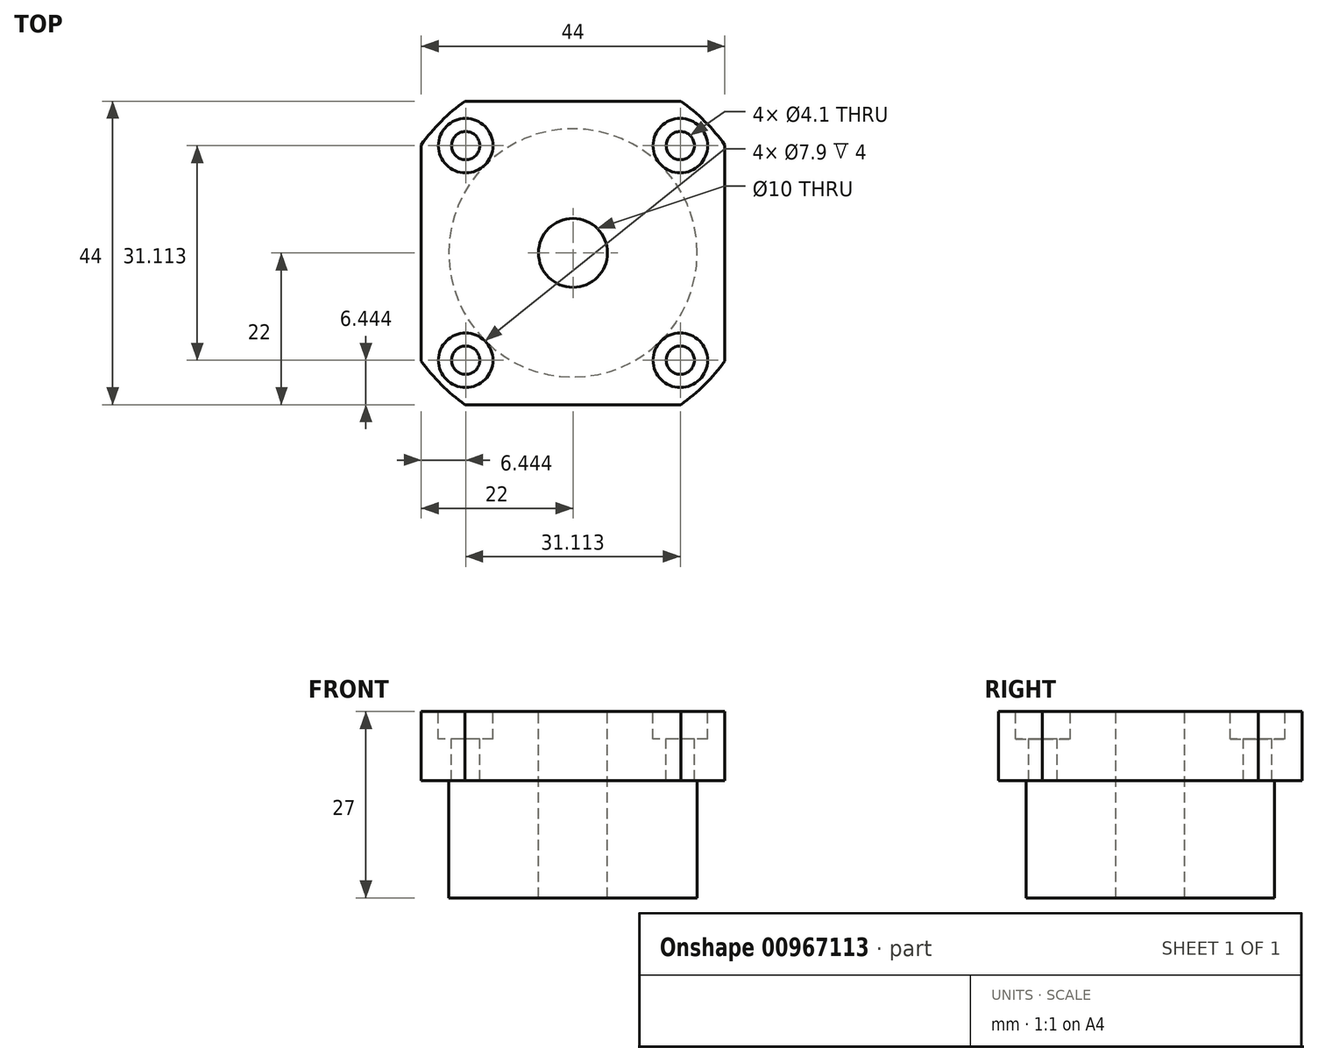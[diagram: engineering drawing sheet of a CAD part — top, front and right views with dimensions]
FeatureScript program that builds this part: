
annotation { "Feature Type Name" : "Feature", "Feature Type Description" : "" }
export const myFeature = defineFeature(function(context is Context, id is Id, definition is map)
    precondition{}
    {
        {
            var Q0;
            Q0=qCreatedBy(makeId("Top.planeOp"),FACE);
            var sketch = newSketch(context, id + "F0", { "sketchPlane" : qUnion([Q0])});
            skLineSegment(sketch, "E0.bottom", {"start": v(0, 0) * mm, "end": v(44, 0) * mm});
            skLineSegment(sketch, "E0.top", {"start": v(0, -44) * mm, "end": v(44, -44) * mm});
            skLineSegment(sketch, "E0.left", {"start": v(0, 0) * mm, "end": v(0, -44) * mm});
            skLineSegment(sketch, "E0.right", {"start": v(44, 0) * mm, "end": v(44, -44) * mm});
            skCircle(sketch, "E1", {"center": v(22, -22) * mm, "radius": 18 * mm});
            skPoint(sketch, "E1.centerSnap0", {"position": v(22, 0) * mm});
            skPoint(sketch, "E1.centerSnap1", {"position": v(0, -22) * mm});
            skCircle(sketch, "E2", {"center": v(22, -22) * mm, "radius": 27 * mm});
            skCircle(sketch, "E3", {"center": v(22, -22) * mm, "radius": 22 * mm, "construction": true});
            skLineSegment(sketch, "E4", {"start": v(22, -22) * mm, "end": v(0, 0) * mm, "construction": true});
            skCircle(sketch, "E5", {"center": v(6.44, -6.44) * mm, "radius": 2.05 * mm});
            skCircle(sketch, "E6", {"center": v(6.44, -6.44) * mm, "radius": 3.95 * mm});
            skCircle(sketch, "E7.1.0", {"center": v(6.44, -37.56) * mm, "radius": 2.05 * mm});
            skCircle(sketch, "E7.1.1", {"center": v(6.44, -37.56) * mm, "radius": 3.95 * mm});
            skCircle(sketch, "E7.2.0", {"center": v(37.56, -37.56) * mm, "radius": 2.05 * mm});
            skCircle(sketch, "E7.2.1", {"center": v(37.56, -37.56) * mm, "radius": 3.95 * mm});
            skCircle(sketch, "E7.3.0", {"center": v(37.56, -6.44) * mm, "radius": 2.05 * mm});
            skCircle(sketch, "E7.3.1", {"center": v(37.56, -6.44) * mm, "radius": 3.95 * mm});
            skCircle(sketch, "E8", {"center": v(22, -22) * mm, "radius": 5 * mm});
            skSolve(sketch);
        }
        {
            var Q0;
            Q0=makeQuery(id+"F0.imprint","IMPRINT",FACE,{"disambiguationData":[TD([[makeQuery(id+"F0.imprint","IMPRINT",EDGE,{"derivedFrom":sQuery(id+"F0.wireOp",EDGE,"E1")}),1.0]])]});
            extrude(context, id + "F1", {"entities" : qUnion([Q0]), "oppositeDirection" : true, "depth" : 27 * mm, "offsetDistance" : 25 * mm});
        }
        {
            var Q0;
            {var subQ10=sQuery(id+"F0.wireOp",EDGE,"E6");Q0=makeQuery(id+"F0.imprint","IMPRINT",FACE,{"disambiguationData":[TD([[makeQuery(id+"F0.imprint","IMPRINT",EDGE,{"derivedFrom":subQ10}),-1.0]])]});}
            var Q1;
            Q1=makeQuery(id+"F0.imprint","IMPRINT",FACE,{"disambiguationData":[TD([[makeQuery(id+"F0.imprint","IMPRINT",EDGE,{"derivedFrom":sQuery(id+"F0.wireOp",EDGE,"E5")}),-1.0]])]});
            var Q2;
            Q2=makeQuery(id+"F0.imprint","IMPRINT",FACE,{"disambiguationData":[TD([[makeQuery(id+"F0.imprint","IMPRINT",EDGE,{"derivedFrom":sQuery(id+"F0.wireOp",EDGE,"E7.3.0")}),-1.0]])]});
            var Q3;
            Q3=makeQuery(id+"F0.imprint","IMPRINT",FACE,{"disambiguationData":[TD([[makeQuery(id+"F0.imprint","IMPRINT",EDGE,{"derivedFrom":sQuery(id+"F0.wireOp",EDGE,"E7.2.0")}),-1.0]])]});
            var Q4;
            Q4=makeQuery(id+"F0.imprint","IMPRINT",FACE,{"disambiguationData":[TD([[makeQuery(id+"F0.imprint","IMPRINT",EDGE,{"derivedFrom":sQuery(id+"F0.wireOp",EDGE,"E7.1.0")}),-1.0]])]});
            extrude(context, id + "F2", {"entities" : qUnion([Q0, Q1, Q2, Q3, Q4]), "operationType" : NewBodyOperationType.ADD, "oppositeDirection" : true, "depth" : 10 * mm, "offsetDistance" : 25 * mm});
        }
        {
            var Q0;
            Q0=makeQuery(id+"F0.imprint","IMPRINT",FACE,{"disambiguationData":[TD([[makeQuery(id+"F0.imprint","IMPRINT",EDGE,{"derivedFrom":sQuery(id+"F0.wireOp",EDGE,"E5")}),-1.0]])]});
            var Q1;
            Q1=makeQuery(id+"F0.imprint","IMPRINT",FACE,{"disambiguationData":[TD([[makeQuery(id+"F0.imprint","IMPRINT",EDGE,{"derivedFrom":sQuery(id+"F0.wireOp",EDGE,"E7.3.0")}),-1.0]])]});
            var Q2;
            Q2=makeQuery(id+"F0.imprint","IMPRINT",FACE,{"disambiguationData":[TD([[makeQuery(id+"F0.imprint","IMPRINT",EDGE,{"derivedFrom":sQuery(id+"F0.wireOp",EDGE,"E7.2.0")}),-1.0]])]});
            var Q3;
            Q3=makeQuery(id+"F0.imprint","IMPRINT",FACE,{"disambiguationData":[TD([[makeQuery(id+"F0.imprint","IMPRINT",EDGE,{"derivedFrom":sQuery(id+"F0.wireOp",EDGE,"E7.1.0")}),-1.0]])]});
            extrude(context, id + "F3", {"entities" : qUnion([Q0, Q1, Q2, Q3]), "operationType" : NewBodyOperationType.REMOVE, "oppositeDirection" : true, "depth" : 4 * mm, "offsetDistance" : 25 * mm});
        }
    });
